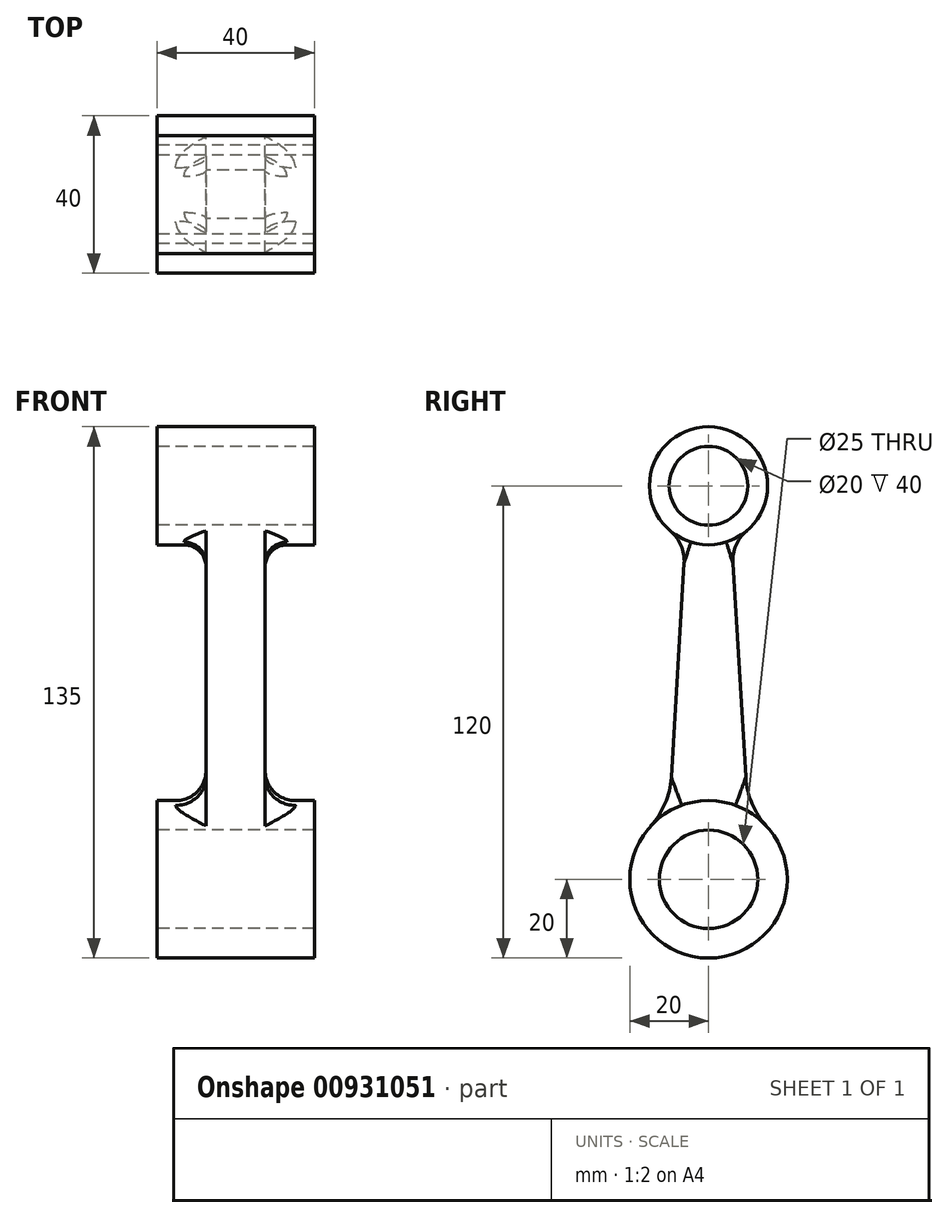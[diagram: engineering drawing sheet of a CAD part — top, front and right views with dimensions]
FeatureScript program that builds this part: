
annotation { "Feature Type Name" : "Feature", "Feature Type Description" : "" }
export const myFeature = defineFeature(function(context is Context, id is Id, definition is map)
    precondition{}
    {
        {
            var Q0;
            Q0=qCreatedBy(makeId("Right.planeOp"),FACE);
            var sketch = newSketch(context, id + "F0", { "sketchPlane" : qUnion([Q0])});
            skCircle(sketch, "E0", {"center": v(0, 0) * mm, "radius": 12.5 * mm});
            skArc(sketch, "E1", {"start": v(-10, 17.32) * mm, "mid": v(0, -20) * mm, "end": v(10, 17.32) * mm});
            skLineSegment(sketch, "E2", {"start": v(-5.84, 86.18) * mm, "end": v(-10, 17.32) * mm});
            skLineSegment(sketch, "E3", {"start": v(10, 17.32) * mm, "end": v(5.84, 86.18) * mm});
            skArc(sketch, "E4", {"start": v(5.84, 86.18) * mm, "mid": v(0, 115) * mm, "end": v(-5.84, 86.18) * mm});
            skPoint(sketch, "E4.centerSnap0", {"position": v(0, 100) * mm});
            skPoint(sketch, "E5", {"position": v(-5, 100) * mm});
            skPoint(sketch, "E6", {"position": v(5, 100) * mm});
            skCircle(sketch, "E7", {"center": v(0, 100) * mm, "radius": 10 * mm});
            skSolve(sketch);
        }
        {
            var Q0;
            Q0=makeQuery(id+"F0.imprint","IMPRINT",FACE,{"disambiguationData":[TD([[makeQuery(id+"F0.imprint","IMPRINT",EDGE,{"derivedFrom":sQuery(id+"F0.wireOp",EDGE,"E0")}),-1.0]])]});
            extrude(context, id + "F1", {"entities" : qUnion([Q0]), "depth" : 15 * mm, "offsetDistance" : 25 * mm, "symmetric" : true});
        }
        {
            var Q0;
            Q0=makeQuery(id+"F1.opExtrude","SWEPT_EDGE",EDGE,{"disambiguationData":[OSD([sQuery(id+"F0.wireOp",EDGE,"E1"),sQuery(id+"F0.wireOp",EDGE,"E3")])]});
            var Q1;
            Q1=makeQuery(id+"F1.opExtrude","SWEPT_EDGE",EDGE,{"disambiguationData":[OSD([sQuery(id+"F0.wireOp",EDGE,"E1"),sQuery(id+"F0.wireOp",EDGE,"E2")])]});
            fillet(context, id + "F2", {"entities" : qUnion([Q0, Q1]), "radius" : 20 * mm, "tangentPropagation" : true, "allowEdgeOverflow" : false});
        }
        {
            var Q0;
            Q0=makeQuery(id+"F1.opExtrude","SWEPT_EDGE",EDGE,{"disambiguationData":[OSD([sQuery(id+"F0.wireOp",EDGE,"E2"),sQuery(id+"F0.wireOp",EDGE,"E4")])]});
            var Q1;
            Q1=makeQuery(id+"F1.opExtrude","SWEPT_EDGE",EDGE,{"disambiguationData":[OSD([sQuery(id+"F0.wireOp",EDGE,"E3"),sQuery(id+"F0.wireOp",EDGE,"E4")])]});
            fillet(context, id + "F3", {"entities" : qUnion([Q0, Q1]), "radius" : 10 * mm, "tangentPropagation" : true, "allowEdgeOverflow" : false});
        }
        {
            var Q0;
            Q0=qCreatedBy(makeId("Right.planeOp"),FACE);
            var sketch = newSketch(context, id + "F4", { "sketchPlane" : qUnion([Q0])});
            skCircle(sketch, "E8", {"center": v(0, 100) * mm, "radius": 15 * mm});
            skCircle(sketch, "E9.0", {"center": v(0, 100) * mm, "radius": 10 * mm});
            skCircle(sketch, "E10.0", {"center": v(0, 0) * mm, "radius": 12.5 * mm});
            skCircle(sketch, "E11", {"center": v(0, 0) * mm, "radius": 20 * mm});
            skSolve(sketch);
        }
        {
            var Q0;
            Q0 = qSketchRegion(id + "F4", true);
            extrude(context, id + "F5", {"entities" : qUnion([Q0]), "operationType" : NewBodyOperationType.ADD, "depth" : 40 * mm, "offsetDistance" : 25 * mm, "symmetric" : true});
        }
        {
            var Q0;
            Q0=makeQuery(id+"F5.boolean.opBoolean","INTERSECT",EDGE,{"derivedFrom":[makeQuery(id+"F1.opExtrude","CAP_FACE",FACE,{"disambiguationData":[OSD([sQuery(id+"F0.wireOp",EDGE,"E0"),sQuery(id+"F0.wireOp",EDGE,"E1"),sQuery(id+"F0.wireOp",EDGE,"E2"),sQuery(id+"F0.wireOp",EDGE,"E3"),sQuery(id+"F0.wireOp",EDGE,"E4"),sQuery(id+"F0.wireOp",EDGE,"E7")])],"isStart":false}),makeQuery(id+"F5.opExtrude","SWEPT_FACE",FACE,{"disambiguationData":[OSD([sQuery(id+"F4.wireOp",EDGE,"E8")])]})]});
            var Q1;
            Q1=makeQuery(id+"F5.boolean.opBoolean","INTERSECT",EDGE,{"derivedFrom":[makeQuery(id+"F1.opExtrude","CAP_FACE",FACE,{"disambiguationData":[OSD([sQuery(id+"F0.wireOp",EDGE,"E0"),sQuery(id+"F0.wireOp",EDGE,"E1"),sQuery(id+"F0.wireOp",EDGE,"E2"),sQuery(id+"F0.wireOp",EDGE,"E3"),sQuery(id+"F0.wireOp",EDGE,"E4"),sQuery(id+"F0.wireOp",EDGE,"E7")])],"isStart":true}),makeQuery(id+"F5.opExtrude","SWEPT_FACE",FACE,{"disambiguationData":[OSD([sQuery(id+"F4.wireOp",EDGE,"E8")])]})]});
            fillet(context, id + "F6", {"entities" : qUnion([Q0, Q1]), "radius" : 5.6 * mm, "tangentPropagation" : true, "allowEdgeOverflow" : false});
        }
        {
            var Q0;
            Q0=makeQuery(id+"F5.boolean.opBoolean","INTERSECT",EDGE,{"derivedFrom":[makeQuery(id+"F1.opExtrude","CAP_FACE",FACE,{"disambiguationData":[OSD([sQuery(id+"F0.wireOp",EDGE,"E0"),sQuery(id+"F0.wireOp",EDGE,"E1"),sQuery(id+"F0.wireOp",EDGE,"E2"),sQuery(id+"F0.wireOp",EDGE,"E3"),sQuery(id+"F0.wireOp",EDGE,"E4"),sQuery(id+"F0.wireOp",EDGE,"E7")])],"isStart":false}),makeQuery(id+"F5.opExtrude","SWEPT_FACE",FACE,{"disambiguationData":[OSD([sQuery(id+"F4.wireOp",EDGE,"E11")])]})]});
            var Q1;
            Q1=makeQuery(id+"F5.boolean.opBoolean","INTERSECT",EDGE,{"derivedFrom":[makeQuery(id+"F1.opExtrude","CAP_FACE",FACE,{"disambiguationData":[OSD([sQuery(id+"F0.wireOp",EDGE,"E0"),sQuery(id+"F0.wireOp",EDGE,"E1"),sQuery(id+"F0.wireOp",EDGE,"E2"),sQuery(id+"F0.wireOp",EDGE,"E3"),sQuery(id+"F0.wireOp",EDGE,"E4"),sQuery(id+"F0.wireOp",EDGE,"E7")])],"isStart":true}),makeQuery(id+"F5.opExtrude","SWEPT_FACE",FACE,{"disambiguationData":[OSD([sQuery(id+"F4.wireOp",EDGE,"E11")])]})]});
            fillet(context, id + "F7", {"entities" : qUnion([Q0, Q1]), "radius" : 7.7 * mm, "tangentPropagation" : true, "allowEdgeOverflow" : false});
        }
    });
